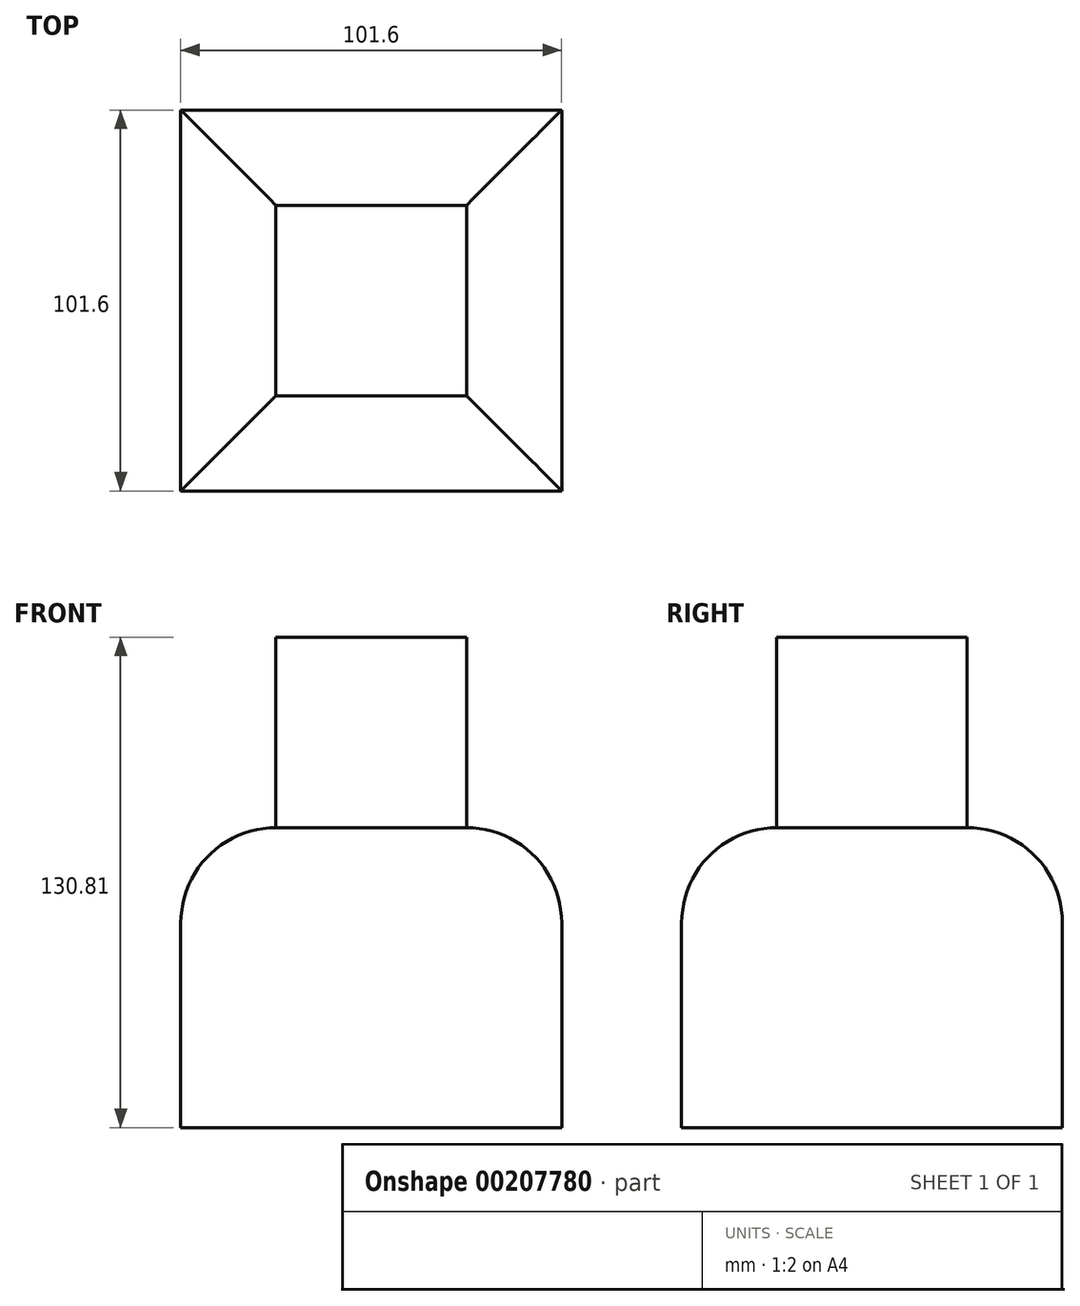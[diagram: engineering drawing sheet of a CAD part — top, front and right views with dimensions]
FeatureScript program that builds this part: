
annotation { "Feature Type Name" : "Feature", "Feature Type Description" : "" }
export const myFeature = defineFeature(function(context is Context, id is Id, definition is map)
    precondition{}
    {
        {
            var Q0;
            Q0=qCreatedBy(makeId("Top.planeOp"),FACE);
            var sketch = newSketch(context, id + "F0", { "sketchPlane" : qUnion([Q0])});
            skLineSegment(sketch, "E0.bottom", {"start": v(-32.92, 63.82) * mm, "end": v(68.68, 63.82) * mm});
            skLineSegment(sketch, "E0.top", {"start": v(-32.92, -37.78) * mm, "end": v(68.68, -37.78) * mm});
            skLineSegment(sketch, "E0.left", {"start": v(-32.92, 63.82) * mm, "end": v(-32.92, -37.78) * mm});
            skLineSegment(sketch, "E0.right", {"start": v(68.68, 63.82) * mm, "end": v(68.68, -37.78) * mm});
            skSolve(sketch);
        }
        {
            var Q0;
            Q0=makeQuery(id+"F0.imprint","IMPRINT",FACE,{"disambiguationData":[TD([[makeQuery(id+"F0.imprint","IMPRINT",EDGE,{"derivedFrom":sQuery(id+"F0.wireOp",EDGE,"E0.bottom")}),-1.0]])]});
            extrude(context, id + "F1", {"entities" : qUnion([Q0]), "depth" : 80 * mm, "offsetDistance" : 25.4 * mm});
        }
        {
            var Q0;
            Q0=makeQuery(id+"F1.opExtrude","CAP_EDGE",EDGE,{"disambiguationData":[OSD([sQuery(id+"F0.wireOp",EDGE,"E0.top")])],"isStart":false});
            var Q1;
            Q1=makeQuery(id+"F1.opExtrude","CAP_EDGE",EDGE,{"disambiguationData":[OSD([sQuery(id+"F0.wireOp",EDGE,"E0.left")])],"isStart":false});
            var Q2;
            Q2=makeQuery(id+"F1.opExtrude","CAP_EDGE",EDGE,{"disambiguationData":[OSD([sQuery(id+"F0.wireOp",EDGE,"E0.bottom")])],"isStart":false});
            var Q3;
            Q3=makeQuery(id+"F1.opExtrude","CAP_EDGE",EDGE,{"disambiguationData":[OSD([sQuery(id+"F0.wireOp",EDGE,"E0.right")])],"isStart":false});
            fillet(context, id + "F2", {"entities" : qUnion([Q0, Q1, Q2, Q3]), "radius" : 25.4 * mm, "tangentPropagation" : true, "allowEdgeOverflow" : false});
        }
        {
            var Q0;
            Q0=makeQuery(id+"F1.opExtrude","CAP_FACE",FACE,{"disambiguationData":[OSD([sQuery(id+"F0.wireOp",EDGE,"E0.bottom"),sQuery(id+"F0.wireOp",EDGE,"E0.top"),sQuery(id+"F0.wireOp",EDGE,"E0.left"),sQuery(id+"F0.wireOp",EDGE,"E0.right")])],"isStart":false});
            extrude(context, id + "F3", {"entities" : qUnion([Q0]), "operationType" : NewBodyOperationType.ADD, "depth" : 50.8 * mm, "offsetDistance" : 25.4 * mm});
        }
    });
